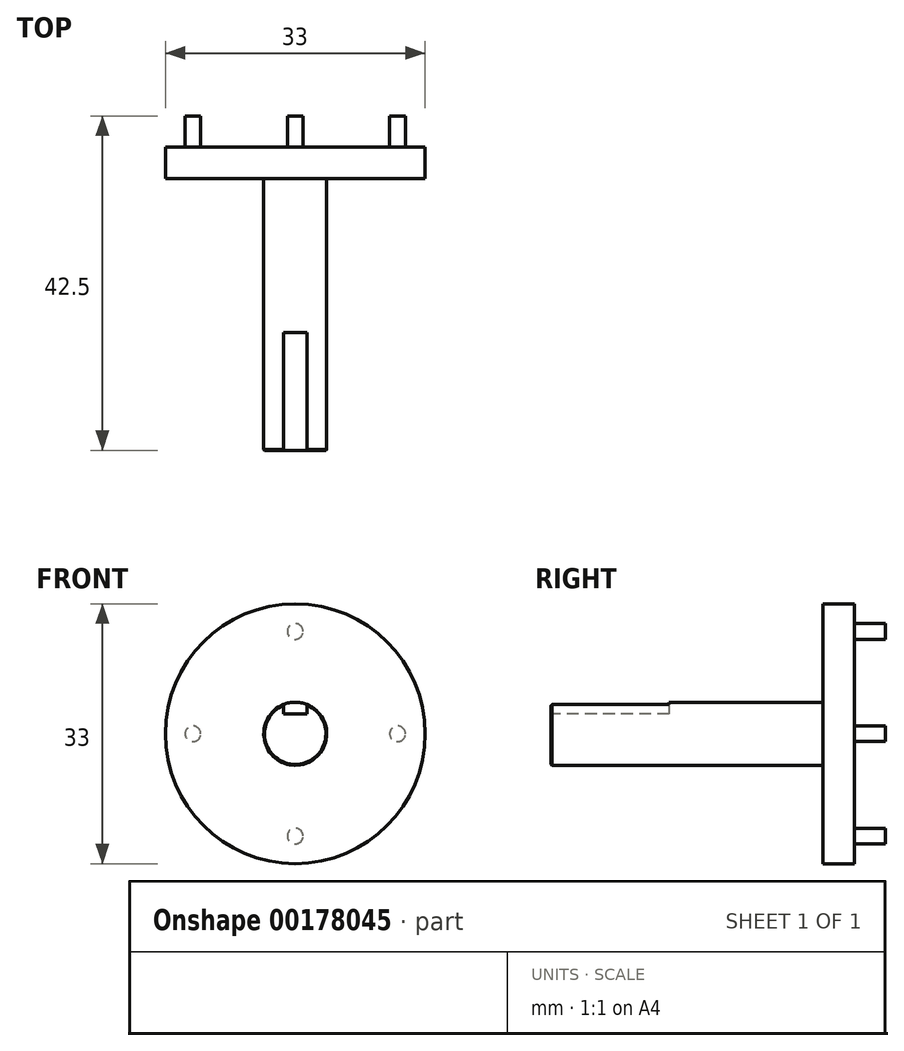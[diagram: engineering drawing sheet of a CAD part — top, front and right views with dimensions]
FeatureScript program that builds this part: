
annotation { "Feature Type Name" : "Feature", "Feature Type Description" : "" }
export const myFeature = defineFeature(function(context is Context, id is Id, definition is map)
    precondition{}
    {
        {
            var Q0;
            Q0=qCreatedBy(makeId("Front.planeOp"),FACE);
            var sketch = newSketch(context, id + "F0", { "sketchPlane" : qUnion([Q0])});
            skCircle(sketch, "E0", {"center": v(0, 0) * mm, "radius": 4 * mm});
            skSolve(sketch);
        }
        {
            var Q0;
            Q0=qSketchRegion(id+"F0",true);
            extrude(context, id + "F1", {"entities" : qUnion([Q0]), "oppositeDirection" : true, "depth" : 28 * mm});
        }
        {
            var Q0;
            Q0=makeQuery(id+"F1.opExtrude","CAP_EDGE",EDGE,{"disambiguationData":[OSD([sQuery(id+"F0.wireOp",EDGE,"E0")])],"isStart":true});
            var Q1;
            Q1=makeQuery(id+"FUtoNcgm9d2VMST_1.boolean.opBoolean","COPY",EDGE,{"derivedFrom":makeQuery(id+"FUtoNcgm9d2VMST_1.opExtrude","SWEPT_EDGE",EDGE,{"disambiguationData":[OSD([sQuery(id+"FhsX1SKP70KWPpT_1.wireOp",EDGE,"66dfabca-b6ee-49d4-a843-992de31440f3.top"),sQuery(id+"FhsX1SKP70KWPpT_1.wireOp",EDGE,"66dfabca-b6ee-49d4-a843-992de31440f3.left")])]})});
            chamfer(context, id + "F2", {"entities" : qUnion([Q0, Q1]), "width" : 0.1 * mm, "tangentPropagation" : true});
        }
        {
            var Q0;
            Q0=makeQuery(id+"F1.opExtrude","CAP_FACE",FACE,{"disambiguationData":[OSD([sQuery(id+"F0.wireOp",EDGE,"E0")])],"isStart":false});
            var sketch = newSketch(context, id + "F3", { "sketchPlane" : qUnion([Q0])});
            skCircle(sketch, "E1", {"center": v(0, 0) * mm, "radius": 4 * mm});
            skSolve(sketch);
        }
        {
            var Q0;
            Q0=qSketchRegion(id+"F3",true);
            extrude(context, id + "F4", {"entities" : qUnion([Q0]), "operationType" : NewBodyOperationType.ADD, "depth" : 6.5 * mm});
        }
        {
            var Q0;
            Q0=makeQuery(id+"F4.opExtrude","CAP_FACE",FACE,{"disambiguationData":[OSD([sQuery(id+"F3.wireOp",EDGE,"E1")])],"isStart":false});
            var sketch = newSketch(context, id + "F5", { "sketchPlane" : qUnion([Q0])});
            skCircle(sketch, "E2", {"center": v(0, 0) * mm, "radius": 16.5 * mm});
            skSolve(sketch);
        }
        {
            var Q0;
            Q0=qSketchRegion(id+"F5",true);
            extrude(context, id + "F6", {"entities" : qUnion([Q0]), "operationType" : NewBodyOperationType.ADD, "depth" : 4 * mm});
        }
        {
            var Q0;
            Q0=makeQuery(id+"F6.opExtrude","CAP_FACE",FACE,{"disambiguationData":[OSD([sQuery(id+"F5.wireOp",EDGE,"E2")])],"isStart":false});
            var sketch = newSketch(context, id + "F7", { "sketchPlane" : qUnion([Q0])});
            skLineSegment(sketch, "E3", {"start": v(0, 0) * mm, "end": v(0, 14.3) * mm, "construction": true});
            skCircle(sketch, "E4", {"center": v(0, 13) * mm, "radius": 1 * mm});
            skCircle(sketch, "E5.1.0", {"center": v(-13, 0) * mm, "radius": 1 * mm});
            skCircle(sketch, "E5.2.0", {"center": v(0, -13) * mm, "radius": 1 * mm});
            skPoint(sketch, "E5.center", {"position": v(0, 0) * mm});
            skCircle(sketch, "E6.1.3.0", {"center": v(13, 0) * mm, "radius": 1 * mm});
            skSolve(sketch);
        }
        {
            var Q0;
            Q0=qSketchRegion(id+"F7",true);
            extrude(context, id + "F8", {"entities" : qUnion([Q0]), "operationType" : NewBodyOperationType.ADD, "depth" : 4 * mm});
        }
        {
            var Q0;
            Q0=makeQuery(id+"F1.opExtrude","CAP_FACE",FACE,{"disambiguationData":[OSD([sQuery(id+"F0.wireOp",EDGE,"E0")])],"isStart":true});
            var sketch = newSketch(context, id + "F9", { "sketchPlane" : qUnion([Q0])});
            skLineSegment(sketch, "E7.bottom", {"start": v(-1.5, 4) * mm, "end": v(1.5, 4) * mm});
            skLineSegment(sketch, "E7.top", {"start": v(-1.5, 2.5) * mm, "end": v(1.5, 2.5) * mm});
            skLineSegment(sketch, "E7.left", {"start": v(-1.5, 4) * mm, "end": v(-1.5, 2.5) * mm});
            skLineSegment(sketch, "E7.right", {"start": v(1.5, 4) * mm, "end": v(1.5, 2.5) * mm});
            skSolve(sketch);
        }
        {
            var Q0;
            Q0 = qSketchRegion(id + "F9", true);
            extrude(context, id + "F10", {"entities" : qUnion([Q0]), "operationType" : NewBodyOperationType.REMOVE, "oppositeDirection" : true, "depth" : 15 * mm});
        }
    });
